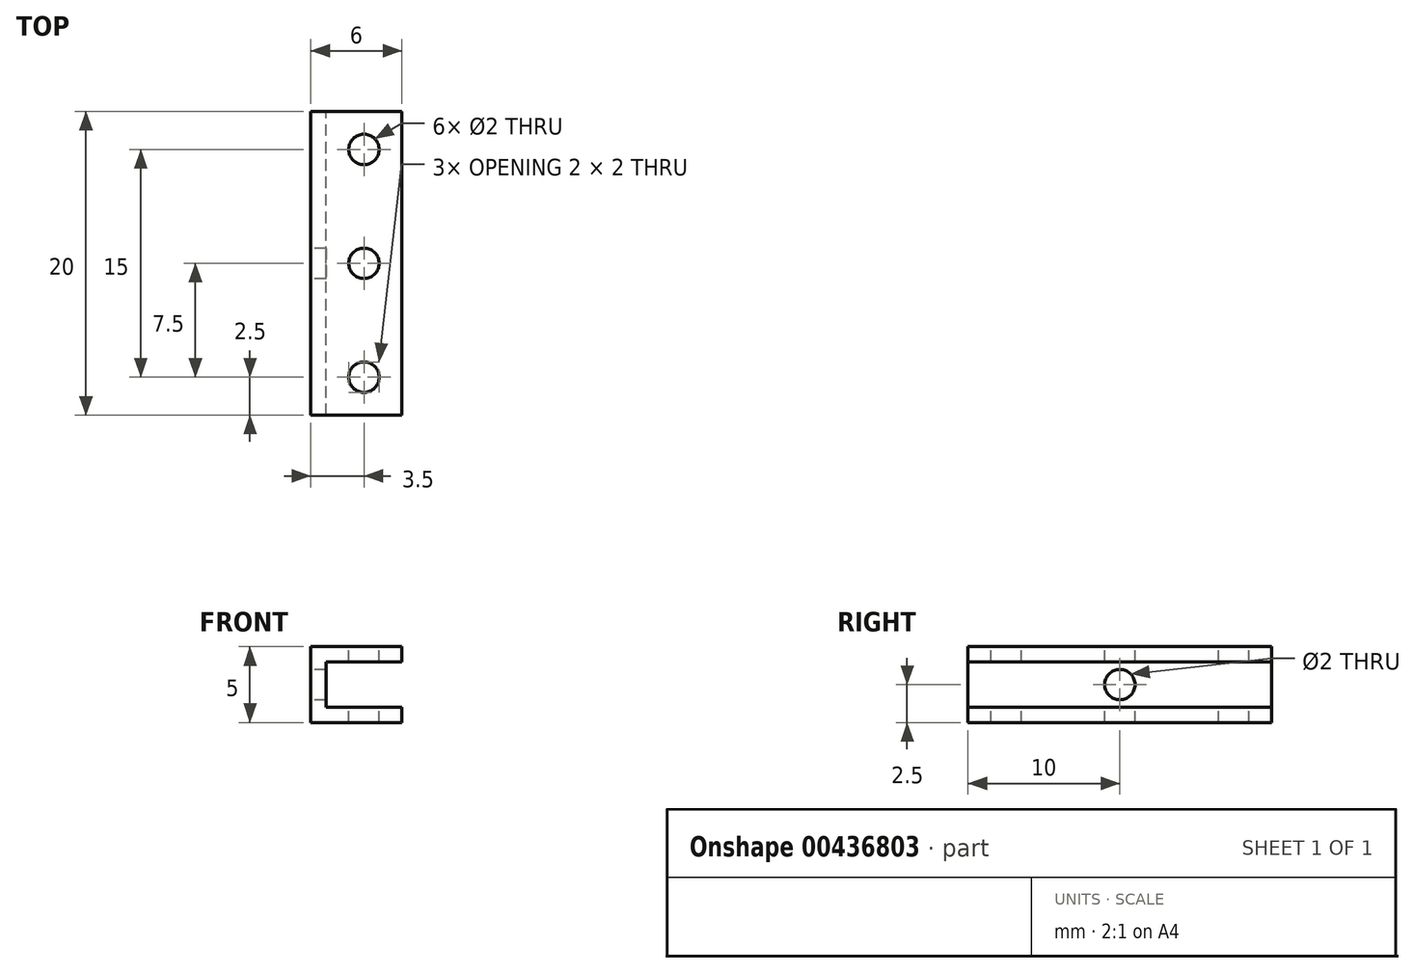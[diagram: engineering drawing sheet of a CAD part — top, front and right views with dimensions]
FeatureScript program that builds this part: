
annotation { "Feature Type Name" : "Feature", "Feature Type Description" : "" }
export const myFeature = defineFeature(function(context is Context, id is Id, definition is map)
    precondition{}
    {
        {
            var Q0;
            Q0=qCreatedBy(makeId("Front.planeOp"),FACE);
            var sketch = newSketch(context, id + "F0", { "sketchPlane" : qUnion([Q0])});
            skLineSegment(sketch, "E0.bottom", {"start": v(2.5, 1.5) * mm, "end": v(-2.5, 1.5) * mm});
            skLineSegment(sketch, "E0.top", {"start": v(2.5, -1.5) * mm, "end": v(-2.5, -1.5) * mm});
            skLineSegment(sketch, "E0.right", {"start": v(-2.5, 1.5) * mm, "end": v(-2.5, -1.5) * mm});
            skPoint(sketch, "E0.middle", {"position": v(0, 0) * mm});
            skLineSegment(sketch, "E1.0", {"start": v(2.5, 2.5) * mm, "end": v(-3.5, 2.5) * mm});
            skLineSegment(sketch, "E2.0", {"start": v(-3.5, 2.5) * mm, "end": v(-3.5, -2.5) * mm});
            skLineSegment(sketch, "E3.0", {"start": v(2.5, -2.5) * mm, "end": v(-3.5, -2.5) * mm});
            skLineSegment(sketch, "E4", {"start": v(2.5, 2.5) * mm, "end": v(2.5, 1.5) * mm});
            skLineSegment(sketch, "E5", {"start": v(2.5, -1.5) * mm, "end": v(2.5, -2.5) * mm});
            skSolve(sketch);
        }
        {
            var Q0;
            Q0 = qSketchRegion(id + "F0", true);
            extrude(context, id + "F1", {"entities" : qUnion([Q0]), "depth" : 20 * mm, "symmetric" : true});
        }
        {
            var Q0;
            Q0=qCreatedBy(makeId("Top.planeOp"),FACE);
            var sketch = newSketch(context, id + "F2", { "sketchPlane" : qUnion([Q0])});
            skCircle(sketch, "E6", {"center": v(0, 7.5) * mm, "radius": 1 * mm});
            skCircle(sketch, "E7.MirrorC", {"center": v(0, -7.5) * mm, "radius": 1 * mm});
            skCircle(sketch, "E8", {"center": v(0, 0) * mm, "radius": 1 * mm});
            skSolve(sketch);
        }
        {
            var Q0;
            Q0 = qSketchRegion(id + "F2", true);
            extrude(context, id + "F3", {"entities" : qUnion([Q0]), "operationType" : NewBodyOperationType.REMOVE, "oppositeDirection" : true, "depth" : 5 * mm, "symmetric" : true});
        }
        {
            var Q0;
            Q0=qCreatedBy(makeId("Right.planeOp"),FACE);
            var sketch = newSketch(context, id + "F4", { "sketchPlane" : qUnion([Q0])});
            skCircle(sketch, "E9", {"center": v(0, 0) * mm, "radius": 1 * mm});
            skSolve(sketch);
        }
        {
            var Q0;
            Q0 = qSketchRegion(id + "F4", true);
            extrude(context, id + "F5", {"entities" : qUnion([Q0]), "operationType" : NewBodyOperationType.REMOVE, "depth" : 10 * mm, "symmetric" : true});
        }
    });
